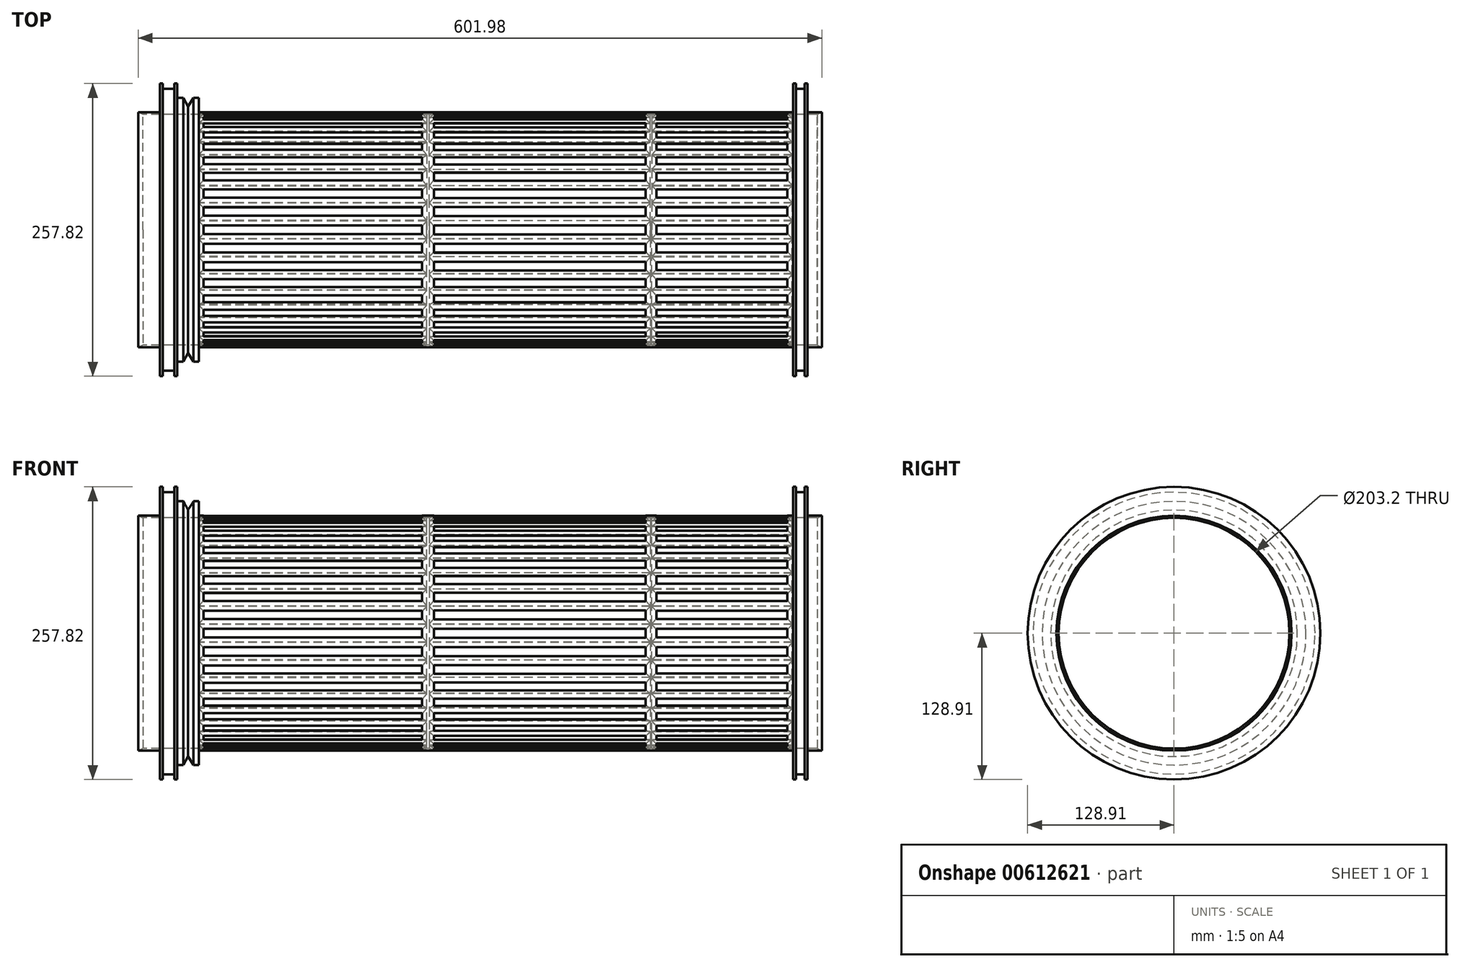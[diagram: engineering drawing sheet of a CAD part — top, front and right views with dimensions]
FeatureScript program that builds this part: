
annotation { "Feature Type Name" : "Feature", "Feature Type Description" : "" }
export const myFeature = defineFeature(function(context is Context, id is Id, definition is map)
    precondition{}
    {
        {
            var Q0;
            Q0=qCreatedBy(makeId("Top.planeOp"),FACE);
            var sketch = newSketch(context, id + "F0", { "sketchPlane" : qUnion([Q0])});
            skLineSegment(sketch, "E0", {"start": v(-353.66, 103.5) * mm, "end": v(-334.6, 103.5) * mm});
            skLineSegment(sketch, "E1", {"start": v(-334.6, 103.5) * mm, "end": v(-334.6, 128.9) * mm});
            skLineSegment(sketch, "E2", {"start": v(-334.6, 128.9) * mm, "end": v(-332.07, 128.9) * mm});
            skLineSegment(sketch, "E3", {"start": v(-319.37, 128.9) * mm, "end": v(-319.37, 103.5) * mm});
            skLineSegment(sketch, "E4", {"start": v(-319.37, 103.5) * mm, "end": v(222.92, 103.5) * mm});
            skLineSegment(sketch, "E5", {"start": v(222.92, 103.5) * mm, "end": v(222.92, 128.9) * mm});
            skLineSegment(sketch, "E6", {"start": v(222.92, 128.9) * mm, "end": v(225.46, 128.9) * mm});
            skLineSegment(sketch, "E7", {"start": v(235.62, 128.9) * mm, "end": v(235.62, 103.5) * mm});
            skLineSegment(sketch, "E8", {"start": v(235.62, 103.5) * mm, "end": v(248.32, 103.5) * mm});
            skLineSegment(sketch, "E9", {"start": v(-353.66, 103.5) * mm, "end": v(-353.66, 101.6) * mm});
            skLineSegment(sketch, "E10", {"start": v(-353.66, 101.6) * mm, "end": v(248.32, 101.6) * mm});
            skLineSegment(sketch, "E11", {"start": v(248.32, 101.6) * mm, "end": v(248.32, 103.5) * mm});
            skLineSegment(sketch, "E12", {"start": v(-332.07, 128.9) * mm, "end": v(-332.07, 124.2) * mm});
            skLineSegment(sketch, "E13", {"start": v(-332.07, 124.2) * mm, "end": v(-321.9, 124.2) * mm});
            skLineSegment(sketch, "E14", {"start": v(-321.9, 124.2) * mm, "end": v(-321.9, 128.9) * mm});
            skLineSegment(sketch, "E15.trimOffspring", {"start": v(-321.9, 128.9) * mm, "end": v(-319.37, 128.9) * mm});
            skLineSegment(sketch, "E16", {"start": v(225.46, 128.9) * mm, "end": v(225.46, 124.2) * mm});
            skLineSegment(sketch, "E17", {"start": v(225.46, 124.2) * mm, "end": v(233.08, 124.2) * mm});
            skLineSegment(sketch, "E18", {"start": v(233.08, 124.2) * mm, "end": v(233.08, 128.9) * mm});
            skLineSegment(sketch, "E19.trimOffspring", {"start": v(233.08, 128.9) * mm, "end": v(235.62, 128.9) * mm});
            skLineSegment(sketch, "E20", {"start": v(-300.16, 103.5) * mm, "end": v(-300.16, 116.2) * mm});
            skPoint(sketch, "E20.endSnap0", {"position": v(-319.37, 116.2) * mm});
            skLineSegment(sketch, "E21", {"start": v(-300.16, 116.2) * mm, "end": v(-304.87, 116.2) * mm});
            skLineSegment(sketch, "E22", {"start": v(-313.74, 116.2) * mm, "end": v(-309.76, 108.6) * mm});
            skPoint(sketch, "E22.endSnap0", {"position": v(-309.76, 116.2) * mm});
            skLineSegment(sketch, "E23", {"start": v(-309.76, 108.6) * mm, "end": v(-304.87, 116.2) * mm});
            skLineSegment(sketch, "E24.trimOffspring", {"start": v(-313.74, 116.2) * mm, "end": v(-319.37, 116.2) * mm});
            skSolve(sketch);
        }
        {
            var Q0;
            Q0=qCreatedBy(makeId("Top.planeOp"),FACE);
            var sketch = newSketch(context, id + "F1", { "sketchPlane" : qUnion([Q0])});
            skLineSegment(sketch, "E25", {"start": v(-76.35, 0) * mm, "end": v(75.96, 0) * mm});
            skSolve(sketch);
        }
        {
            var Q0;
            Q0=makeQuery(id+"F0.imprint","IMPRINT",FACE,{"disambiguationData":[TD([[makeQuery(id+"F0.imprint","IMPRINT",EDGE,{"derivedFrom":sQuery(id+"F0.wireOp",EDGE,"E0")}),-1.0]])]});
            var Q1;
            Q1 = qSketchRegion(id + "F3", true);
            var Q2;
            {var subQ0=sQuery(id+"F0.wireOp",EDGE,"E20");Q2=makeQuery(id+"F0.imprint","IMPRINT",FACE,{"disambiguationData":[TD([[makeQuery(id+"F0.imprint","IMPRINT",EDGE,{"derivedFrom":subQ0}),1.0]])]});}
            var Q3;
            Q3=sQuery(id+"F1.wireOp",EDGE,"E25");
            revolve(context, id + "F2", {"entities" : qUnion([Q0, Q1, Q2]), "axis" : qUnion([Q3]), "revolveType" : RevolveType.FULL});
        }
        {
            var Q0;
            Q0=qCreatedBy(makeId("Top.planeOp"),FACE);
            var sketch = newSketch(context, id + "F3", { "sketchPlane" : qUnion([Q0])});
            skLineSegment(sketch, "E26.bottom", {"start": v(-103.68, -3.81) * mm, "end": v(-296.04, -3.81) * mm});
            skLineSegment(sketch, "E26.top", {"start": v(-103.68, 3.81) * mm, "end": v(-296.04, 3.81) * mm});
            skLineSegment(sketch, "E26.left", {"start": v(-103.68, -3.8) * mm, "end": v(-103.68, 3.81) * mm});
            skPoint(sketch, "E26.middle", {"position": v(-205.28, 0) * mm});
            skLineSegment(sketch, "E27.bottom", {"start": v(93.22, 3.98) * mm, "end": v(-93.22, 3.98) * mm});
            skLineSegment(sketch, "E27.top", {"start": v(93.22, -3.98) * mm, "end": v(-93.22, -3.98) * mm});
            skLineSegment(sketch, "E27.left", {"start": v(93.22, 3.98) * mm, "end": v(93.22, -3.98) * mm});
            skLineSegment(sketch, "E27.right", {"start": v(-93.22, 3.98) * mm, "end": v(-93.22, -3.98) * mm});
            skPoint(sketch, "E27.middle", {"position": v(0, 0) * mm});
            skLineSegment(sketch, "E28.bottom", {"start": v(218.02, -3.81) * mm, "end": v(102.72, -3.81) * mm});
            skLineSegment(sketch, "E28.top", {"start": v(218.02, 3.8) * mm, "end": v(102.72, 3.8) * mm});
            skLineSegment(sketch, "E28.right", {"start": v(102.72, -3.81) * mm, "end": v(102.72, 3.8) * mm});
            skPoint(sketch, "E28.middle", {"position": v(166.22, 0) * mm});
            skLineSegment(sketch, "E29", {"start": v(-296.04, -3.81) * mm, "end": v(-296.04, 3.81) * mm});
            skPoint(sketch, "E30.orphan", {"position": v(-306.88, -3.81) * mm});
            skPoint(sketch, "E31.orphan", {"position": v(-306.88, 3.81) * mm});
            skLineSegment(sketch, "E32", {"start": v(218.02, -3.81) * mm, "end": v(218.02, 3.81) * mm});
            skPoint(sketch, "E28.left.start.orphan", {"position": v(229.72, -3.81) * mm});
            skPoint(sketch, "E33.orphan", {"position": v(229.72, 3.8) * mm});
            skSolve(sketch);
        }
        {
            var Q0;
            Q0 = qSketchRegion(id + "F3", true);
            extrude(context, id + "F4", {"entities" : qUnion([Q0]), "depth" : 114.3 * mm, "offsetDistance" : 25.4 * mm});
        }
        {
            var Q0;
            Q0=makeQuery(id+"F4.opExtrude","SWEPT_BODY",BODY,{"disambiguationData":[OSD([sQuery(id+"F3.wireOp",EDGE,"E26.bottom"),sQuery(id+"F3.wireOp",EDGE,"E26.top"),sQuery(id+"F3.wireOp",EDGE,"E26.left"),sQuery(id+"F3.wireOp",EDGE,"E26.right")])]});
            var Q1;
            Q1=makeQuery(id+"F4.opExtrude","SWEPT_BODY",BODY,{"disambiguationData":[OSD([sQuery(id+"F3.wireOp",EDGE,"E27.bottom"),sQuery(id+"F3.wireOp",EDGE,"E27.top"),sQuery(id+"F3.wireOp",EDGE,"E27.left"),sQuery(id+"F3.wireOp",EDGE,"E27.right")])]});
            var Q2;
            Q2=makeQuery(id+"F4.opExtrude","SWEPT_BODY",BODY,{"disambiguationData":[OSD([sQuery(id+"F3.wireOp",EDGE,"E28.bottom"),sQuery(id+"F3.wireOp",EDGE,"E28.top"),sQuery(id+"F3.wireOp",EDGE,"E28.left"),sQuery(id+"F3.wireOp",EDGE,"E28.right")])]});
            var Q3;
            Q3=makeQuery(id+"F2.opRevolve","SWEPT_EDGE",EDGE,{"disambiguationData":[OSD([sQuery(id+"F0.wireOp",EDGE,"E9"),sQuery(id+"F0.wireOp",EDGE,"E10")])]});
            circularPattern(context, id + "F5", {"operationType" : NewBodyOperationType.REMOVE, "entities" : qUnion([Q0, Q1, Q2]), "axis" : qUnion([Q3]), "angle" : 360 * degree, "instanceCount" : 40, "equalSpace" : true});
        }
        {
            var Q0;
            Q0=makeQuery(id+"F2.opRevolve","SWEPT_FACE",FACE,{"disambiguationData":[OSD([sQuery(id+"F0.wireOp",EDGE,"E10")])]});
            chamfer(context, id + "F6", {"entities" : qUnion([Q0]), "chamferType" : ChamferType.TWO_OFFSETS, "width1" : 4.06 * mm, "oppositeDirection" : false, "width2" : 1.9 * mm});
        }
    });
